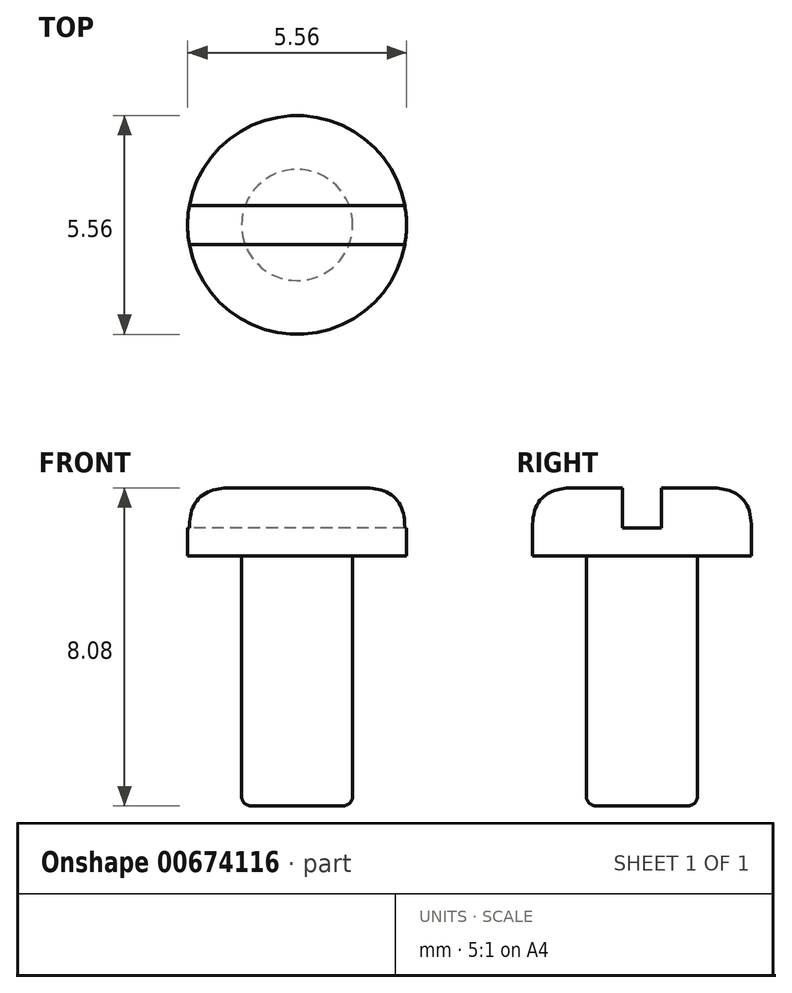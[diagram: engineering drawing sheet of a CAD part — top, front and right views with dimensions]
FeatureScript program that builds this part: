
annotation { "Feature Type Name" : "Feature", "Feature Type Description" : "" }
export const myFeature = defineFeature(function(context is Context, id is Id, definition is map)
    precondition{}
    {
        {
            var Q0;
            Q0=qCreatedBy(makeId("Top.planeOp"),FACE);
            var sketch = newSketch(context, id + "F0", { "sketchPlane" : qUnion([Q0])});
            skCircle(sketch, "E0", {"center": v(0, 0) * mm, "radius": 1.41 * mm});
            skCircle(sketch, "E1", {"center": v(0, 0) * mm, "radius": 2.78 * mm});
            skSolve(sketch);
        }
        {
            var Q0;
            Q0=makeQuery(id+"F0.imprint","IMPRINT",FACE,{"disambiguationData":[TD([[makeQuery(id+"F0.imprint","IMPRINT",EDGE,{"derivedFrom":sQuery(id+"F0.wireOp",EDGE,"E0")}),1.0]])]});
            var Q1;
            Q1=makeQuery(id+"F0.imprint","IMPRINT",FACE,{"disambiguationData":[TD([[makeQuery(id+"F0.imprint","IMPRINT",EDGE,{"derivedFrom":sQuery(id+"F0.wireOp",EDGE,"E0")}),-1.0]])]});
            extrude(context, id + "F1", {"entities" : qUnion([Q0, Q1]), "depth" : 1.73 * mm, "offsetDistance" : 25 * mm});
        }
        {
            var Q0;
            Q0=makeQuery(id+"F0.imprint","IMPRINT",FACE,{"disambiguationData":[TD([[makeQuery(id+"F0.imprint","IMPRINT",EDGE,{"derivedFrom":sQuery(id+"F0.wireOp",EDGE,"E0")}),1.0]])]});
            extrude(context, id + "F2", {"entities" : qUnion([Q0]), "operationType" : NewBodyOperationType.ADD, "oppositeDirection" : true, "depth" : 6.35 * mm, "offsetDistance" : 25 * mm});
        }
        {
            var Q0;
            Q0=makeQuery(id+"F1.opExtrude","CAP_FACE",FACE,{"disambiguationData":[OSD([sQuery(id+"F0.wireOp",EDGE,"E1")])],"isStart":false});
            fillet(context, id + "F3", {"entities" : qUnion([Q0]), "radius" : 1 * mm, "tangentPropagation" : true, "rho" : 0.5, "crossSection" : FilletCrossSection.CONIC, "allowEdgeOverflow" : false});
        }
        {
            var Q0;
            Q0=qCreatedBy(makeId("Right.planeOp"),FACE);
            var sketch = newSketch(context, id + "F4", { "sketchPlane" : qUnion([Q0])});
            skLineSegment(sketch, "E2.bottom", {"start": v(-0.5, 2.74) * mm, "end": v(0.5, 2.74) * mm});
            skLineSegment(sketch, "E2.top", {"start": v(-0.5, 0.71) * mm, "end": v(0.5, 0.71) * mm});
            skLineSegment(sketch, "E2.left", {"start": v(-0.5, 2.74) * mm, "end": v(-0.5, 0.71) * mm});
            skLineSegment(sketch, "E2.right", {"start": v(0.5, 2.74) * mm, "end": v(0.5, 0.71) * mm});
            skPoint(sketch, "E2.middle", {"position": v(0, 1.73) * mm});
            skSolve(sketch);
        }
        {
            var Q0;
            Q0 = qSketchRegion(id + "F4", true);
            extrude(context, id + "F5", {"entities" : qUnion([Q0]), "operationType" : NewBodyOperationType.REMOVE, "depth" : 6 * mm, "offsetDistance" : 25 * mm, "symmetric" : true});
        }
        {
            var Q0;
            Q0=makeQuery(id+"F2.opExtrude","CAP_FACE",FACE,{"disambiguationData":[OSD([sQuery(id+"F0.wireOp",EDGE,"E0")])],"isStart":false});
            fillet(context, id + "F6", {"entities" : qUnion([Q0]), "radius" : 0.25 * mm, "tangentPropagation" : true, "allowEdgeOverflow" : false});
        }
    });
